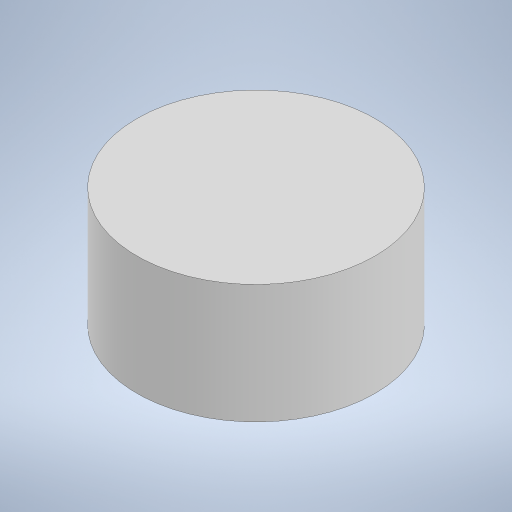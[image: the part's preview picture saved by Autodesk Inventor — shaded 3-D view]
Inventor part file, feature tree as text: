
AUTODESK INVENTOR PART (.ipt)
format: ipt  version: 2023 (Build 270158000, 158)  size: 193,024 bytes
history: native  units: in
note: dims shown in document units (in); Inventor stores cm internally (conversion verified against a paired STEP export)
features: extrude x2, sketch x2
ambient origin geometry x8: Origin, YZ Plane, XZ Plane, XY Plane, X Axis, Y Axis, Z Axis, Center Point
bodies: Solid1 (feature_tree)
feature tree (4):
  extrude  "Extrusion1"  Depth=0.5in TaperAngle=0.0deg
  extrude  "Extrusion2"  Depth=0.3in TaperAngle=0.0deg
  sketch  "Sketch1"  dims[d0=1.0in d1=0.5in d2=0.0in]
  sketch  "Sketch2"  dims[d3=0.25in d4=0.3in d5=0.0in]
